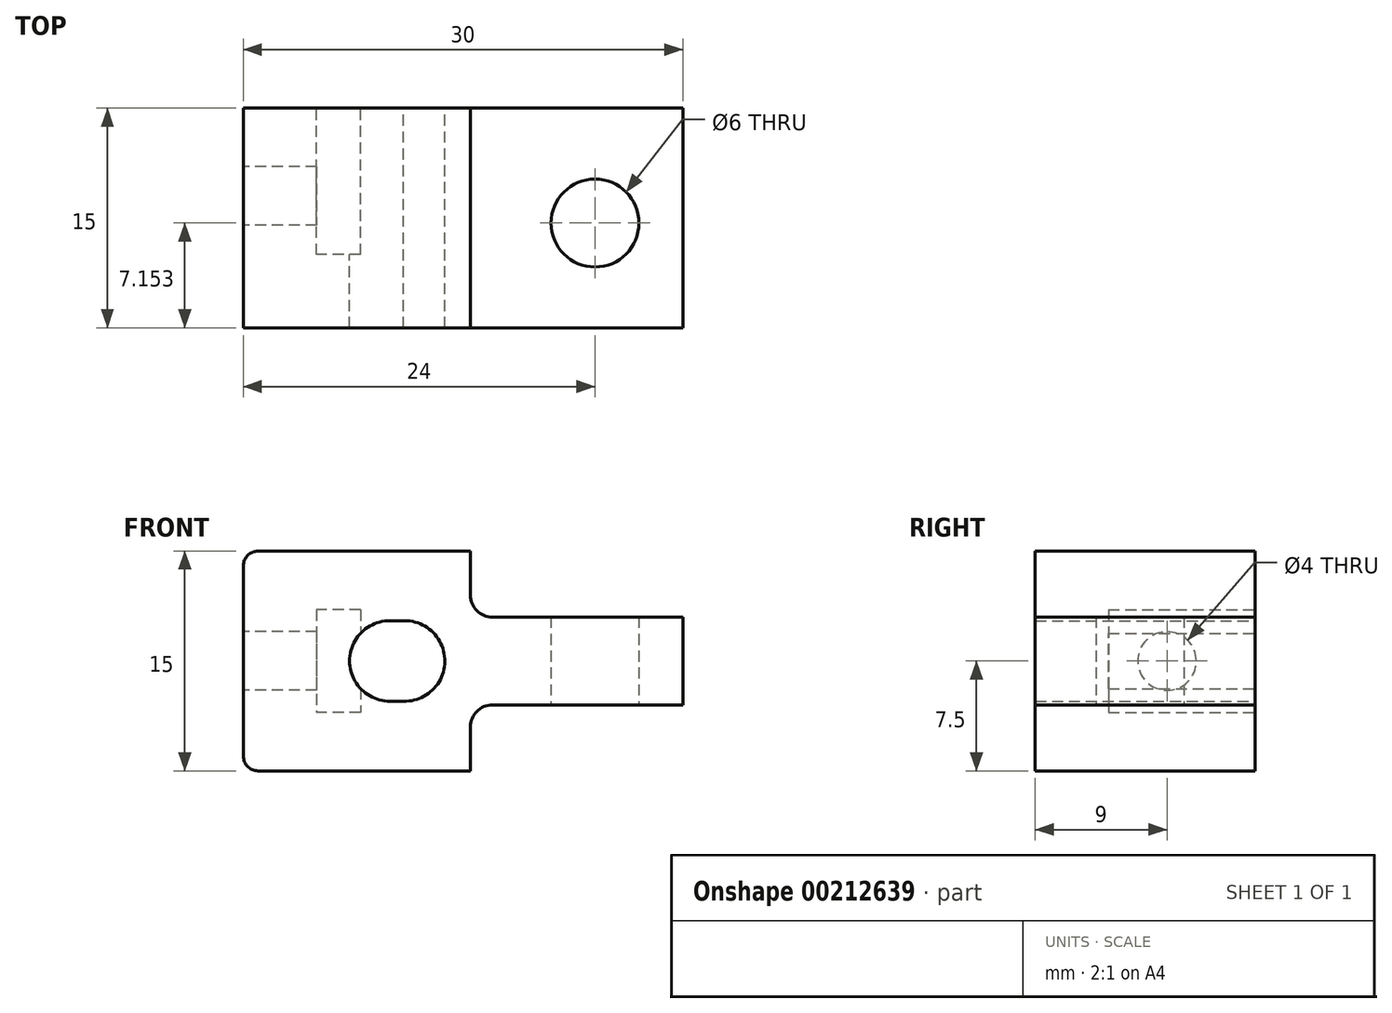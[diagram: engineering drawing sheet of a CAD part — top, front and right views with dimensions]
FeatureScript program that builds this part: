
annotation { "Feature Type Name" : "Feature", "Feature Type Description" : "" }
export const myFeature = defineFeature(function(context is Context, id is Id, definition is map)
    precondition{}
    {
        {
            var Q0;
            Q0=qCreatedBy(makeId("Front.planeOp"),FACE);
            var sketch = newSketch(context, id + "F0", { "sketchPlane" : qUnion([Q0])});
            skLineSegment(sketch, "E0", {"start": v(1, 15) * mm, "end": v(15.5, 15) * mm});
            skLineSegment(sketch, "E1", {"start": v(15.5, 15) * mm, "end": v(15.5, 12) * mm});
            skLineSegment(sketch, "E2", {"start": v(17, 10.5) * mm, "end": v(30, 10.5) * mm});
            skLineSegment(sketch, "E3", {"start": v(30, 10.5) * mm, "end": v(30, 4.5) * mm});
            skLineSegment(sketch, "E4", {"start": v(30, 4.5) * mm, "end": v(17, 4.5) * mm});
            skLineSegment(sketch, "E5", {"start": v(15.5, 3) * mm, "end": v(15.5, 0) * mm});
            skLineSegment(sketch, "E6", {"start": v(15.5, 0) * mm, "end": v(1, 0) * mm});
            skLineSegment(sketch, "E7", {"start": v(0, 1) * mm, "end": v(0, 14) * mm});
            skPoint(sketch, "E8.visualSharp", {"position": v(15.5, 4.5) * mm});
            skArc(sketch, "E8.filletArc", {"start": v(17, 4.5) * mm, "mid": v(15.94, 4.06) * mm, "end": v(15.5, 3) * mm});
            skPoint(sketch, "E9.visualSharp", {"position": v(15.5, 10.5) * mm});
            skArc(sketch, "E9.filletArc", {"start": v(15.5, 12) * mm, "mid": v(15.94, 10.94) * mm, "end": v(17, 10.5) * mm});
            skPoint(sketch, "E10.visualSharp", {"position": v(0, 0) * mm});
            skArc(sketch, "E10.filletArc", {"start": v(0, 1) * mm, "mid": v(0.3, 0.3) * mm, "end": v(1, 0) * mm});
            skPoint(sketch, "E11.visualSharp", {"position": v(0, 15) * mm});
            skArc(sketch, "E11.filletArc", {"start": v(1, 15) * mm, "mid": v(0.3, 14.7) * mm, "end": v(0, 14) * mm});
            skCircle(sketch, "E12", {"center": v(10, 7.5) * mm, "radius": 2.75 * mm});
            skCircle(sketch, "E13", {"center": v(11, 7.5) * mm, "radius": 2.75 * mm});
            skLineSegment(sketch, "E14", {"start": v(10, 10.25) * mm, "end": v(11, 10.25) * mm});
            skLineSegment(sketch, "E15", {"start": v(10, 4.75) * mm, "end": v(11.07, 4.75) * mm});
            skSolve(sketch);
        }
        {
            var Q0;
            Q0=makeQuery(id+"F0.imprint","IMPRINT",FACE,{"disambiguationData":[TD([[makeQuery(id+"F0.imprint","IMPRINT",EDGE,{"derivedFrom":sQuery(id+"F0.wireOp",EDGE,"E0")}),-1.0]])]});
            extrude(context, id + "F1", {"entities" : qUnion([Q0]), "depth" : 15 * mm});
        }
        {
            var Q0;
            Q0=qCreatedBy(makeId("Top.planeOp"),FACE);
            var sketch = newSketch(context, id + "F2", { "sketchPlane" : qUnion([Q0])});
            skCircle(sketch, "E16", {"center": v(24, -7.85) * mm, "radius": 3 * mm});
            skSolve(sketch);
        }
        {
            var Q0;
            Q0 = qSketchRegion(id + "F2", true);
            extrude(context, id + "F3", {"entities" : qUnion([Q0]), "operationType" : NewBodyOperationType.REMOVE, "endBound" : BoundingType.THROUGH_ALL, "depth" : 25 * mm});
        }
        {
            var Q0;
            Q0=makeQuery(id+"F1.opExtrude","CAP_FACE",FACE,{"disambiguationData":[OSD([sQuery(id+"F0.wireOp",EDGE,"E0"),sQuery(id+"F0.wireOp",EDGE,"E1"),sQuery(id+"F0.wireOp",EDGE,"E2"),sQuery(id+"F0.wireOp",EDGE,"E3"),sQuery(id+"F0.wireOp",EDGE,"E4"),sQuery(id+"F0.wireOp",EDGE,"E5"),sQuery(id+"F0.wireOp",EDGE,"E6"),sQuery(id+"F0.wireOp",EDGE,"E7"),sQuery(id+"F0.wireOp",EDGE,"E8.filletArc"),sQuery(id+"F0.wireOp",EDGE,"E9.filletArc"),sQuery(id+"F0.wireOp",EDGE,"E10.filletArc"),sQuery(id+"F0.wireOp",EDGE,"E11.filletArc"),sQuery(id+"F0.wireOp",EDGE,"E12")])],"isStart":true});
            var sketch = newSketch(context, id + "F4", { "sketchPlane" : qUnion([Q0])});
            skLineSegment(sketch, "E17.bottom", {"start": v(-8, 11) * mm, "end": v(-5, 11) * mm});
            skLineSegment(sketch, "E17.top", {"start": v(-8, 4) * mm, "end": v(-5, 4) * mm});
            skLineSegment(sketch, "E17.left", {"start": v(-8, 11) * mm, "end": v(-8, 4) * mm});
            skLineSegment(sketch, "E17.right", {"start": v(-5, 11) * mm, "end": v(-5, 4) * mm});
            skSolve(sketch);
        }
        {
            var Q0;
            Q0 = qSketchRegion(id + "F4", true);
            extrude(context, id + "F5", {"entities" : qUnion([Q0]), "operationType" : NewBodyOperationType.REMOVE, "oppositeDirection" : true, "depth" : 10 * mm});
        }
        {
            var Q0;
            Q0=makeQuery(id+"F1.opExtrude","SWEPT_FACE",FACE,{"disambiguationData":[OSD([sQuery(id+"F0.wireOp",EDGE,"E7")])]});
            var sketch = newSketch(context, id + "F6", { "sketchPlane" : qUnion([Q0])});
            skCircle(sketch, "E18", {"center": v(6, 7.5) * mm, "radius": 2 * mm});
            skSolve(sketch);
        }
        {
            var Q0;
            Q0 = qSketchRegion(id + "F6", true);
            extrude(context, id + "F7", {"entities" : qUnion([Q0]), "operationType" : NewBodyOperationType.REMOVE, "oppositeDirection" : true, "depth" : 5 * mm});
        }
    });
